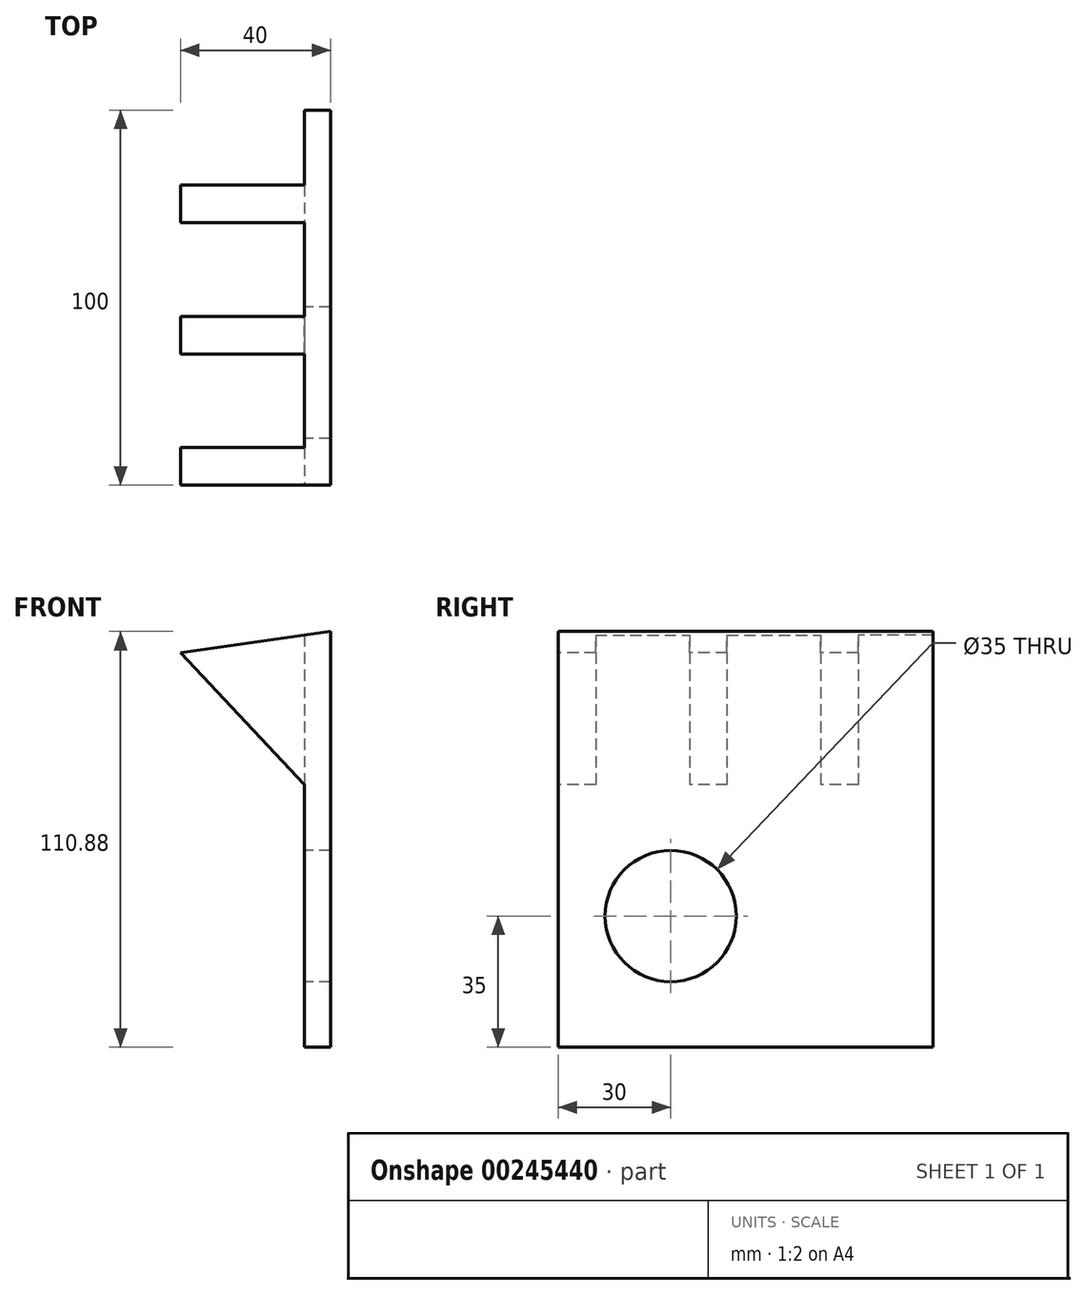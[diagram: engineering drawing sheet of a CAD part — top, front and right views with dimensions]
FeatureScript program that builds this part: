
annotation { "Feature Type Name" : "Feature", "Feature Type Description" : "" }
export const myFeature = defineFeature(function(context is Context, id is Id, definition is map)
    precondition{}
    {
        {
            var Q0;
            Q0=qCreatedBy(makeId("Front.planeOp"),FACE);
            var sketch = newSketch(context, id + "F0", { "sketchPlane" : qUnion([Q0])});
            skLineSegment(sketch, "E0", {"start": v(0, 0) * mm, "end": v(0, 90) * mm});
            skLineSegment(sketch, "E1", {"start": v(0, 90) * mm, "end": v(148.54, 110.88) * mm});
            skLineSegment(sketch, "E2", {"start": v(148.54, 110.88) * mm, "end": v(148.54, 0) * mm});
            skLineSegment(sketch, "E3", {"start": v(148.54, 0) * mm, "end": v(0, 0) * mm});
            skSolve(sketch);
        }
        {
            var Q0;
            Q0=qSketchRegion(id+"F0",true);
            extrude(context, id + "F1", {"entities" : qUnion([Q0]), "depth" : 100 * mm});
        }
        {
            var Q0;
            Q0=makeQuery(id+"F1.opExtrude","CAP_FACE",FACE,{"disambiguationData":[OSD([sQuery(id+"F0.wireOp",EDGE,"E0"),sQuery(id+"F0.wireOp",EDGE,"E1"),sQuery(id+"F0.wireOp",EDGE,"E2"),sQuery(id+"F0.wireOp",EDGE,"E3")])],"isStart":false});
            var sketch = newSketch(context, id + "F2", { "sketchPlane" : qUnion([Q0])});
            skLineSegment(sketch, "E4", {"start": v(148.54, 0) * mm, "end": v(108.54, 0) * mm});
            skLineSegment(sketch, "E5", {"start": v(0, 90) * mm, "end": v(108.54, 105.25) * mm});
            skLineSegment(sketch, "E6", {"start": v(141.54, 0) * mm, "end": v(141.54, 70) * mm});
            skLineSegment(sketch, "E7", {"start": v(141.54, 70) * mm, "end": v(108.54, 105.25) * mm});
            skLineSegment(sketch, "E8", {"start": v(0, 90) * mm, "end": v(0, 0) * mm});
            skLineSegment(sketch, "E9", {"start": v(0, 0) * mm, "end": v(108.54, 0) * mm});
            skSolve(sketch);
        }
        {
            var Q0;
            Q0=qSketchRegion(id+"F2",true);
            extrude(context, id + "F3", {"entities" : qUnion([Q0]), "operationType" : NewBodyOperationType.REMOVE, "oppositeDirection" : true, "depth" : 100 * mm});
        }
        {
            var Q0;
            Q0=makeQuery(id+"F1.opExtrude","SWEPT_FACE",FACE,{"disambiguationData":[OSD([sQuery(id+"F0.wireOp",EDGE,"E3")])]});
            var sketch = newSketch(context, id + "F4", { "sketchPlane" : qUnion([Q0])});
            skLineSegment(sketch, "E10", {"start": v(141.54, 100) * mm, "end": v(141.54, 90) * mm});
            skLineSegment(sketch, "E11.bottom", {"start": v(141.54, 90) * mm, "end": v(97.2, 90) * mm});
            skLineSegment(sketch, "E11.top", {"start": v(141.54, 65) * mm, "end": v(97.2, 65) * mm});
            skLineSegment(sketch, "E11.left", {"start": v(141.54, 90) * mm, "end": v(141.54, 65) * mm});
            skLineSegment(sketch, "E11.right", {"start": v(97.2, 90) * mm, "end": v(97.2, 65) * mm});
            skLineSegment(sketch, "E12", {"start": v(141.54, 65) * mm, "end": v(141.54, 55) * mm});
            skLineSegment(sketch, "E13.bottom", {"start": v(141.54, 55) * mm, "end": v(96.55, 55) * mm});
            skLineSegment(sketch, "E13.top", {"start": v(141.54, 30) * mm, "end": v(96.55, 30) * mm});
            skLineSegment(sketch, "E13.left", {"start": v(141.54, 55) * mm, "end": v(141.54, 30) * mm});
            skLineSegment(sketch, "E13.right", {"start": v(96.55, 55) * mm, "end": v(96.55, 30) * mm});
            skLineSegment(sketch, "E14", {"start": v(141.54, 30) * mm, "end": v(141.54, 20) * mm});
            skLineSegment(sketch, "E15.bottom", {"start": v(141.54, 20) * mm, "end": v(95.9, 20) * mm});
            skLineSegment(sketch, "E15.top", {"start": v(141.54, -7.83) * mm, "end": v(95.9, -7.83) * mm});
            skLineSegment(sketch, "E15.left", {"start": v(141.54, 20) * mm, "end": v(141.54, -7.83) * mm});
            skLineSegment(sketch, "E15.right", {"start": v(95.9, 20) * mm, "end": v(95.9, -7.83) * mm});
            skSolve(sketch);
        }
        {
            var Q0;
            Q0=qSketchRegion(id+"F4",true);
            extrude(context, id + "F5", {"entities" : qUnion([Q0]), "operationType" : NewBodyOperationType.REMOVE, "oppositeDirection" : true, "depth" : 114 * mm});
        }
        {
            var Q0;
            Q0=makeQuery(id+"F5.boolean.opBoolean","MERGE",FACE,{"derivedFrom":[makeQuery(id+"F3.boolean.opBoolean","COPY",FACE,{"derivedFrom":makeQuery(id+"F3.opExtrude","SWEPT_FACE",FACE,{"disambiguationData":[OSD([sQuery(id+"F2.wireOp",EDGE,"E6")])]})}),makeQuery(id+"F5.opExtrude","SWEPT_FACE",FACE,{"disambiguationData":[OSD([sQuery(id+"F4.wireOp",EDGE,"E11.left")])]}),makeQuery(id+"F5.opExtrude","SWEPT_FACE",FACE,{"disambiguationData":[OSD([sQuery(id+"F4.wireOp",EDGE,"E13.left")])]}),makeQuery(id+"F5.opExtrude","SWEPT_FACE",FACE,{"disambiguationData":[OSD([sQuery(id+"F4.wireOp",EDGE,"E15.left")])]})]});
            var sketch = newSketch(context, id + "F6", { "sketchPlane" : qUnion([Q0])});
            skLineSegment(sketch, "E16", {"start": v(100, 0) * mm, "end": v(100, 70) * mm});
            skLineSegment(sketch, "E17", {"start": v(100, 35) * mm, "end": v(40, 35) * mm});
            skCircle(sketch, "E18", {"center": v(70, 35) * mm, "radius": 17.5 * mm});
            skSolve(sketch);
        }
        {
            var Q0;
            Q0=qSketchRegion(id+"F6",true);
            extrude(context, id + "F7", {"entities" : qUnion([Q0]), "operationType" : NewBodyOperationType.REMOVE, "oppositeDirection" : true, "depth" : 25 * mm});
        }
    });
